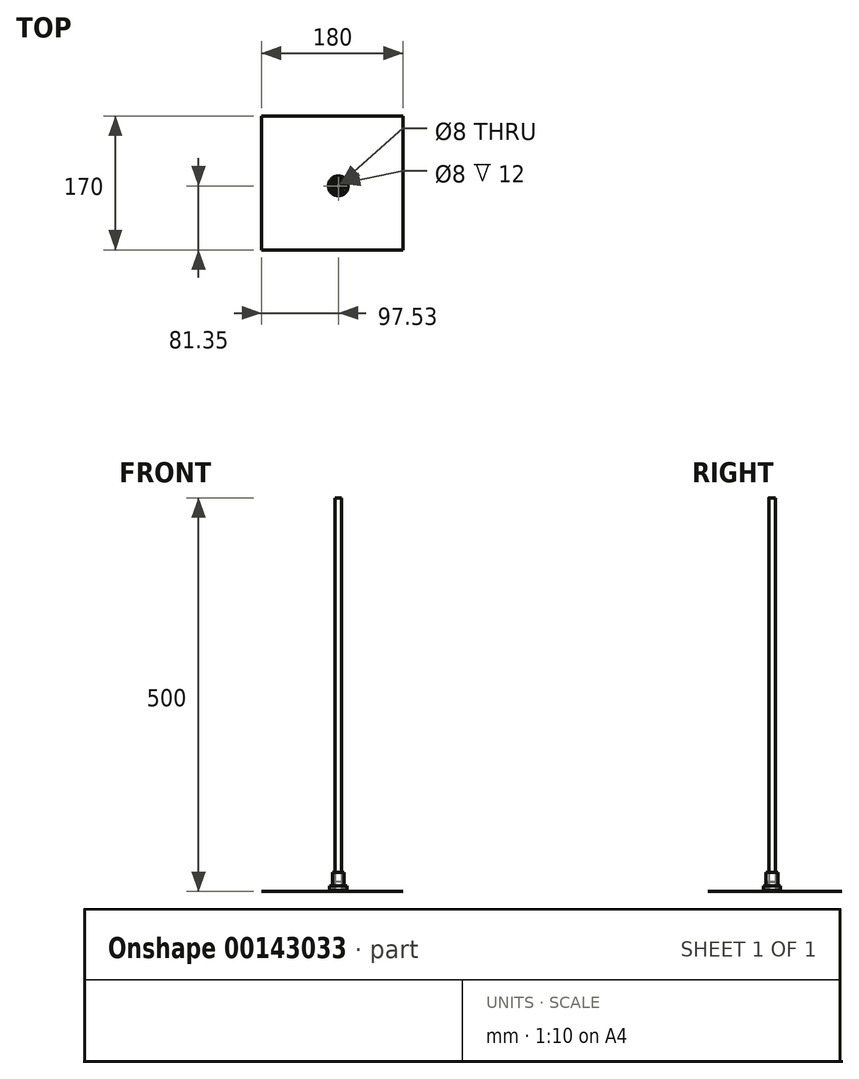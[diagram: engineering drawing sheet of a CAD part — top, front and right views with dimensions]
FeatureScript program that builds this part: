
annotation { "Feature Type Name" : "Feature", "Feature Type Description" : "" }
export const myFeature = defineFeature(function(context is Context, id is Id, definition is map)
    precondition{}
    {
        {
            var Q0;
            Q0=qCreatedBy(makeId("Top.planeOp"),FACE);
            var sketch = newSketch(context, id + "F0", { "sketchPlane" : qUnion([Q0])});
            skCircle(sketch, "E0", {"center": v(0, 0) * mm, "radius": 12.5 * mm});
            skCircle(sketch, "E1", {"center": v(0, 0) * mm, "radius": 11 * mm});
            skCircle(sketch, "E2", {"center": v(0, 0) * mm, "radius": 4 * mm});
            skSolve(sketch);
        }
        {
            var Q0;
            Q0=makeQuery(id+"F0.imprint","IMPRINT",FACE,{"disambiguationData":[TD([[makeQuery(id+"F0.imprint","IMPRINT",EDGE,{"derivedFrom":sQuery(id+"F0.wireOp",EDGE,"E1")}),1.0]])]});
            extrude(context, id + "F1", {"entities" : qUnion([Q0]), "depth" : 7 * mm});
        }
        {
            var Q0;
            Q0=makeQuery(id+"F0.imprint","IMPRINT",FACE,{"disambiguationData":[TD([[makeQuery(id+"F0.imprint","IMPRINT",EDGE,{"derivedFrom":sQuery(id+"F0.wireOp",EDGE,"E0")}),1.0]])]});
            extrude(context, id + "F2", {"entities" : qUnion([Q0]), "operationType" : NewBodyOperationType.ADD, "depth" : 1.5 * mm});
        }
        {
            var Q0;
            Q0=qCreatedBy(makeId("Top.planeOp"),FACE);
            var sketch = newSketch(context, id + "F3", { "sketchPlane" : qUnion([Q0])});
            skCircle(sketch, "E3", {"center": v(0, 0) * mm, "radius": 2 * mm});
            skCircle(sketch, "E4", {"center": v(0, 0) * mm, "radius": 6.5 * mm});
            skCircle(sketch, "E5", {"center": v(0, 0) * mm, "radius": 7.5 * mm});
            skSolve(sketch);
        }
        {
            var Q0;
            Q0=makeQuery(id+"F3.imprint","IMPRINT",FACE,{"disambiguationData":[TD([[makeQuery(id+"F3.imprint","IMPRINT",EDGE,{"derivedFrom":sQuery(id+"F3.wireOp",EDGE,"E3")}),-1.0]])]});
            extrude(context, id + "F4", {"entities" : qUnion([Q0]), "depth" : 5 * mm});
        }
        {
            var Q0;
            Q0=makeQuery(id+"F3.imprint","IMPRINT",FACE,{"disambiguationData":[TD([[makeQuery(id+"F3.imprint","IMPRINT",EDGE,{"derivedFrom":sQuery(id+"F3.wireOp",EDGE,"E4")}),-1.0]])]});
            extrude(context, id + "F5", {"entities" : qUnion([Q0]), "operationType" : NewBodyOperationType.ADD, "depth" : 1 * mm});
        }
        {
            var Q0;
            Q0=qCreatedBy(makeId("Top.planeOp"),FACE);
            var sketch = newSketch(context, id + "F6", { "sketchPlane" : qUnion([Q0])});
            skCircle(sketch, "E6", {"center": v(0, 0) * mm, "radius": 4 * mm});
            skCircle(sketch, "E7", {"center": v(0, 0) * mm, "radius": 5 * mm});
            skSolve(sketch);
        }
        {
            var Q0;
            Q0=qSketchRegion(id+"F6",true);
            var Q1;
            Q1=makeQuery(id+"F6.imprint","IMPRINT",FACE,{"disambiguationData":[TD([[makeQuery(id+"F6.imprint","IMPRINT",EDGE,{"derivedFrom":sQuery(id+"F6.wireOp",EDGE,"E6")}),-1.0]])]});
            extrude(context, id + "F7", {"entities" : qUnion([Q0, Q1]), "depth" : 12 * mm});
        }
        {
            var Q0;
            Q0=qCreatedBy(makeId("Top.planeOp"),FACE);
            var sketch = newSketch(context, id + "F8", { "sketchPlane" : qUnion([Q0])});
            skCircle(sketch, "E8", {"center": v(0, 0) * mm, "radius": 4 * mm});
            skSolve(sketch);
        }
        {
            var Q0;
            Q0=qSketchRegion(id+"F8",true);
            extrude(context, id + "F9", {"entities" : qUnion([Q0]), "depth" : 500 * mm});
        }
        {
            var Q0;
            Q0=makeQuery(id+"F8.imprint","IMPRINT",FACE,{"disambiguationData":[TD([[makeQuery(id+"F8.imprint","IMPRINT",EDGE,{"derivedFrom":sQuery(id+"F8.wireOp",EDGE,"E8")}),1.0]])]});
            var Q1;
            Q1=sQuery(id+"F8.wireOp",EDGE,"E8");
            extrude(context, id + "F10", {"entities" : qUnion([Q0]), "surfaceEntities" : qUnion([Q1]), "depth" : 200 * mm});
        }
        {
            var Q0;
            Q0=qCreatedBy(makeId("Top.planeOp"),FACE);
            var sketch = newSketch(context, id + "F11", { "sketchPlane" : qUnion([Q0])});
            skCircle(sketch, "E9.cCircle", {"center": v(0, 0) * mm, "radius": 3.9 * mm, "construction": true});
            skLineSegment(sketch, "E9.0", {"start": v(2.25, -3.9) * mm, "end": v(-2.25, -3.9) * mm});
            skLineSegment(sketch, "E9.1", {"start": v(-2.25, -3.9) * mm, "end": v(-4.5, 0) * mm});
            skLineSegment(sketch, "E9.2", {"start": v(-4.5, 0) * mm, "end": v(-2.25, 3.9) * mm});
            skLineSegment(sketch, "E9.3", {"start": v(-2.25, 3.9) * mm, "end": v(2.25, 3.9) * mm});
            skLineSegment(sketch, "E9.4", {"start": v(2.25, 3.9) * mm, "end": v(4.5, 0) * mm});
            skLineSegment(sketch, "E9.5", {"start": v(4.5, 0) * mm, "end": v(2.25, -3.9) * mm});
            skPoint(sketch, "E9.0.midPoint", {"position": v(0, -3.9) * mm});
            skSolve(sketch);
        }
        {
            var Q0;
            Q0=qSketchRegion(id+"F11",true);
            var Q1;
            Q1=makeQuery(id+"F11.imprint","IMPRINT",FACE,{"disambiguationData":[TD([[makeQuery(id+"F11.imprint","IMPRINT",EDGE,{"derivedFrom":sQuery(id+"F11.wireOp",EDGE,"E9.0")}),-1.0]])]});
            extrude(context, id + "F12", {"entities" : qUnion([Q0, Q1]), "depth" : 4 * mm});
        }
        {
            var Q0;
            Q0=makeQuery(id+"F12.opExtrude","CAP_FACE",FACE,{"disambiguationData":[OSD([sQuery(id+"F11.wireOp",EDGE,"E9.0"),sQuery(id+"F11.wireOp",EDGE,"E9.1"),sQuery(id+"F11.wireOp",EDGE,"E9.2"),sQuery(id+"F11.wireOp",EDGE,"E9.3"),sQuery(id+"F11.wireOp",EDGE,"E9.4"),sQuery(id+"F11.wireOp",EDGE,"E9.5")])],"isStart":false});
            var sketch = newSketch(context, id + "F13", { "sketchPlane" : qUnion([Q0])});
            skCircle(sketch, "E10", {"center": v(0, 0) * mm, "radius": 2.5 * mm});
            skSolve(sketch);
        }
        {
            var Q0;
            Q0=qSketchRegion(id+"F13",true);
            var Q1;
            Q1=makeQuery(id+"F13.imprint","IMPRINT",FACE,{"disambiguationData":[TD([[makeQuery(id+"F13.imprint","IMPRINT",EDGE,{"derivedFrom":sQuery(id+"F13.wireOp",EDGE,"E10")}),1.0]])]});
            extrude(context, id + "F14", {"entities" : qUnion([Q0, Q1]), "operationType" : NewBodyOperationType.ADD, "depth" : 25 * mm});
        }
        {
            var Q0;
            Q0=qCreatedBy(makeId("Top.planeOp"),FACE);
            var sketch = newSketch(context, id + "F15", { "sketchPlane" : qUnion([Q0])});
            skCircle(sketch, "E11", {"center": v(0, 0) * mm, "radius": 2.75 * mm});
            skSolve(sketch);
        }
        {
            var Q0;
            Q0 = qSketchRegion(id + "F15", true);
            extrude(context, id + "F16", {"entities" : qUnion([Q0]), "depth" : 3 * mm});
        }
        {
            var Q0;
            Q0=makeQuery(id+"F16.opExtrude","CAP_FACE",FACE,{"disambiguationData":[OSD([sQuery(id+"F15.wireOp",EDGE,"E11")])],"isStart":false});
            var sketch = newSketch(context, id + "F17", { "sketchPlane" : qUnion([Q0])});
            skCircle(sketch, "E12", {"center": v(0, 0) * mm, "radius": 1.5 * mm});
            skSolve(sketch);
        }
        {
            var Q0;
            Q0 = qSketchRegion(id + "F17", true);
            extrude(context, id + "F18", {"entities" : qUnion([Q0]), "operationType" : NewBodyOperationType.ADD, "depth" : 20 * mm});
        }
        {
            var Q0;
            Q0=qCreatedBy(makeId("Top.planeOp"),FACE);
            var sketch = newSketch(context, id + "F19", { "sketchPlane" : qUnion([Q0])});
            skCircle(sketch, "E13", {"center": v(0, 0) * mm, "radius": 4 * mm});
            skCircle(sketch, "E14", {"center": v(0, 0) * mm, "radius": 7.5 * mm});
            skSolve(sketch);
        }
        {
            var Q0;
            Q0=makeQuery(id+"F19.imprint","IMPRINT",FACE,{"disambiguationData":[TD([[makeQuery(id+"F19.imprint","IMPRINT",EDGE,{"derivedFrom":sQuery(id+"F19.wireOp",EDGE,"E13")}),-1.0]])]});
            extrude(context, id + "F20", {"entities" : qUnion([Q0]), "depth" : 24 * mm});
        }
        {
            var Q0;
            Q0=qCreatedBy(makeId("Top.planeOp"),FACE);
            var sketch = newSketch(context, id + "F21", { "sketchPlane" : qUnion([Q0])});
            skLineSegment(sketch, "E15.bottom", {"start": v(-97.53, 88.65) * mm, "end": v(82.47, 88.65) * mm});
            skLineSegment(sketch, "E15.top", {"start": v(-97.53, -81.35) * mm, "end": v(82.47, -81.35) * mm});
            skLineSegment(sketch, "E15.left", {"start": v(-97.53, 88.65) * mm, "end": v(-97.53, -81.35) * mm});
            skLineSegment(sketch, "E15.right", {"start": v(82.47, 88.65) * mm, "end": v(82.47, -81.35) * mm});
            skSolve(sketch);
        }
        {
            var Q0;
            Q0=makeQuery(id+"F21.imprint","IMPRINT",FACE,{"disambiguationData":[TD([[makeQuery(id+"F21.imprint","IMPRINT",EDGE,{"derivedFrom":sQuery(id+"F21.wireOp",EDGE,"E15.bottom")}),-1.0]])]});
            extrude(context, id + "F22", {"entities" : qUnion([Q0]), "depth" : 0.1 * mm});
        }
    });
